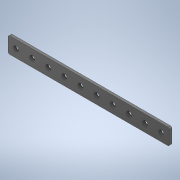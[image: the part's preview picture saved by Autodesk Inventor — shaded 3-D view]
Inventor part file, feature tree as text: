
AUTODESK INVENTOR PART (.ipt)
format: ipt  version: 2020 (Build 240168000, 168)  size: 126,464 bytes
history: native  units: mm
features: extrude x2, sketch x2, pattern_linear x1, fillet x1
ambient origin geometry x8: Origin, YZ Plane, XZ Plane, XY Plane, X Axis, Y Axis, Z Axis, Center Point
bodies: Solid1 (feature_tree)
feature tree (6):
  extrude  "Extrusion1"  Depth=20.0mm
  extrude  "Extrusion2"  Depth=2.0mm
  pattern_linear  "Rectangular Pattern1"  Spacing1=10.0mm  [1 undecoded]
  fillet  "Fillet1"  Radius=10.0mm
  sketch  "Sketch1"  dims[d0=200.0mm d1=20.0mm]
  sketch  "Sketch2"  dims[d3=3.0mm d4=0.0mm d5=6.0mm d6=10.0mm d7=10.0mm d8=3.0mm d9=0.0mm d10=100.0mm d12=20.0mm d13=2.0mm]
note: 1 required parameter value undecoded (feature->parameter linkage not recoverable at this tier; creation-order binding heuristic only, values carry confidence <= 0.55)
